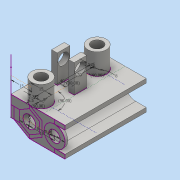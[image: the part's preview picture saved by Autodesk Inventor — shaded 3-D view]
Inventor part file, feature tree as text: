
AUTODESK INVENTOR PART (.ipt)
format: ipt  version: 2016 (Build 200138000, 138)  size: 202,752 bytes
history: native  units: mm
features: extrude x5, sketch x2, hole x2
ambient origin geometry x8: Origin, YZ Plane, XZ Plane, XY Plane, X Axis, Y Axis, Z Axis, Center Point
bodies: Solid1 (feature_tree)
feature tree (9):
  sketch  "Sketch1"  dims[d0=7.0mm d1=18.0mm d2=15.0mm d3=9.0mm d4=8.0mm d6=15.0mm]
  extrude  "Extrusion1"  Depth=15.0mm
  sketch  "Sketch2"  dims[d7=58.0mm d8=0.0mm d9=15.0mm d10=6.5mm d11=90.0deg d12=8.0mm d13=40.0mm d14=90.0deg d15=8.0mm d16=2.576473mm d17=2.726812mm d18=20.0mm d19=90.0deg d20=4.0mm d21=180.0deg d22=15.0mm d23=0.0mm d24=20.0mm d25=0.0mm d26=14.0mm d27=4.5mm d28=8.0mm d29=6.0mm d30=4.0mm d31=2.0mm d32=90.0deg d33=8.0mm d34=20.594885mm d35=4.0mm d36=0.0mm d37=5.0mm d38=5.0mm d39=4.0mm d40=6.0mm d41=4.0mm d42=2.0mm d43=90.0deg d44=8.0mm d45=20.594885mm d46=2.0mm d47=0.0mm]
  extrude  "Extrusion2"  Depth=15.0mm
  extrude  "Extrusion3"  Depth=2.0mm
  hole  "Hole1"  [1 undecoded]
  extrude  "Extrusion4"  Depth=8.0mm
  hole  "Hole2"  [1 undecoded]
  extrude  "Extrusion5"  TaperAngle=90.0deg  [1 undecoded]
note: 3 required parameter values undecoded (feature->parameter linkage not recoverable at this tier; creation-order binding heuristic only, values carry confidence <= 0.55)
